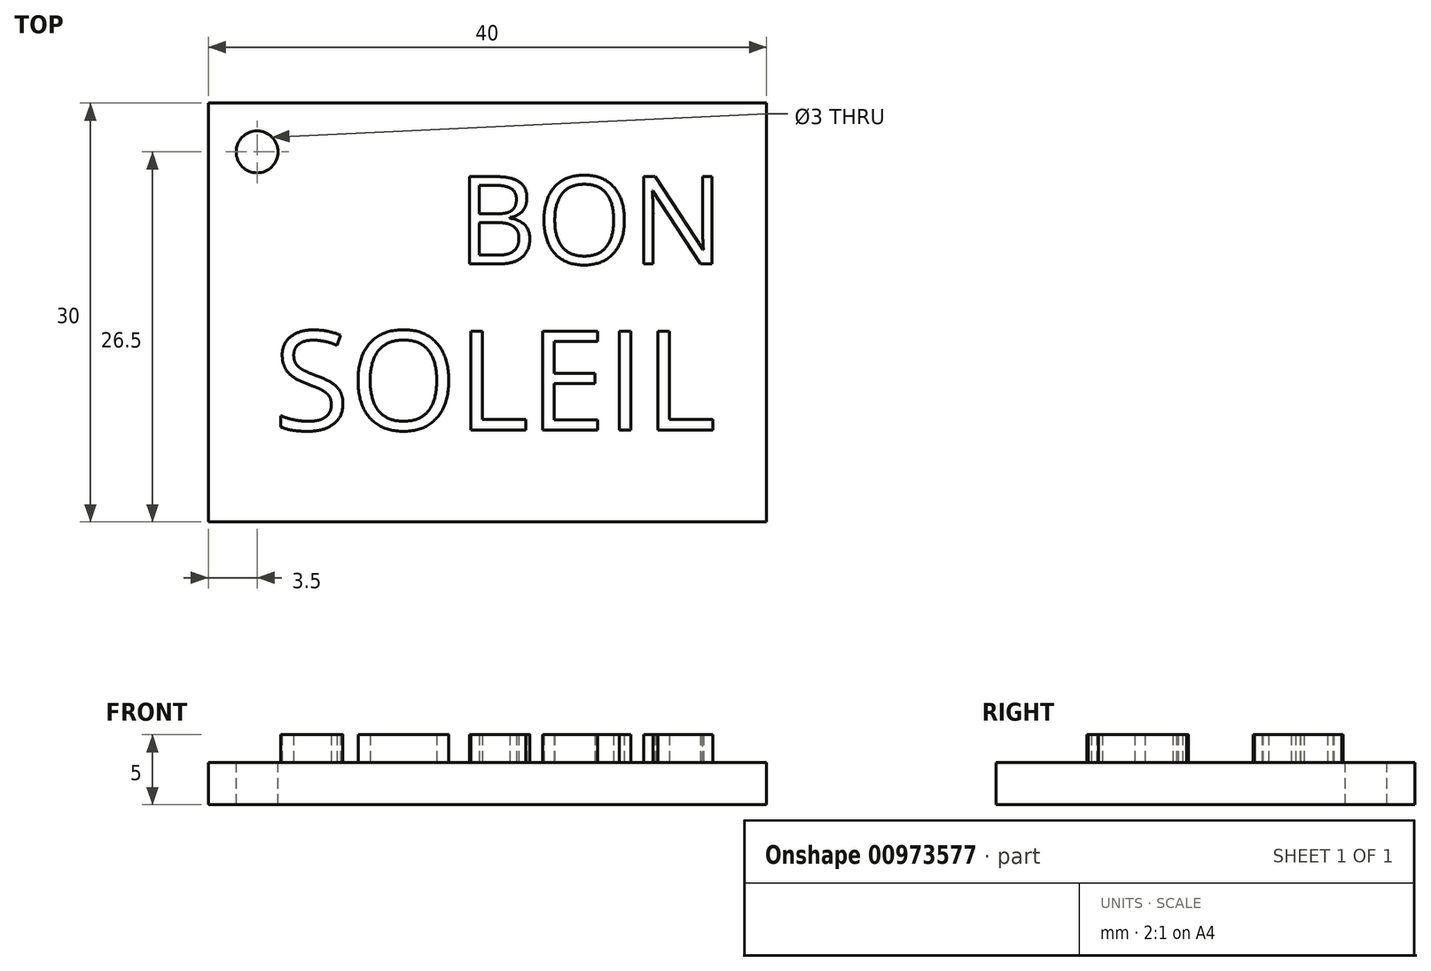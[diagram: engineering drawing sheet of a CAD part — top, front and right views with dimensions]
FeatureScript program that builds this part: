
annotation { "Feature Type Name" : "Feature", "Feature Type Description" : "" }
export const myFeature = defineFeature(function(context is Context, id is Id, definition is map)
    precondition{}
    {
        {
            var Q0;
            Q0=qCreatedBy(makeId("Top.planeOp"),FACE);
            var sketch = newSketch(context, id + "F0", { "sketchPlane" : qUnion([Q0])});
            skLineSegment(sketch, "E0.bottom", {"start": v(0, 0) * mm, "end": v(40, 0) * mm});
            skLineSegment(sketch, "E0.top", {"start": v(0, 30) * mm, "end": v(40, 30) * mm});
            skLineSegment(sketch, "E0.left", {"start": v(0, 0) * mm, "end": v(0, 30) * mm});
            skLineSegment(sketch, "E0.right", {"start": v(40, 0) * mm, "end": v(40, 30) * mm});
            skSolve(sketch);
        }
        {
            var Q0;
            Q0=qSketchRegion(id+"F0",true);
            extrude(context, id + "F1", {"entities" : qUnion([Q0]), "oppositeDirection" : true, "depth" : 3 * mm, "offsetDistance" : 25 * mm});
        }
        {
            var Q0;
            Q0=makeQuery(id+"F1.opExtrude","CAP_FACE",FACE,{"disambiguationData":[OSD([sQuery(id+"F0.wireOp",EDGE,"E0.bottom"),sQuery(id+"F0.wireOp",EDGE,"E0.top"),sQuery(id+"F0.wireOp",EDGE,"E0.left"),sQuery(id+"F0.wireOp",EDGE,"E0.right")])],"isStart":true});
            var sketch = newSketch(context, id + "F2", { "sketchPlane" : qUnion([Q0])});
            skText(sketch, "E1", { "text": "BON", "fontName": "OpenSans-Regular.ttf"});
            skText(sketch, "E2", { "text": "SOLEIL", "fontName": "OpenSans-Regular.ttf"});
            const initialGuessF2  = {"E1": [0.01784, 0.01848, 1, 0, 0.00631], "E2": [0.00469, 0.00658, 1, 0, 0.00713]};
            skSetInitialGuess(sketch, initialGuessF2);
            skSolve(sketch);
        }
        {
            var Q0;
            Q0=qSketchRegion(id+"F2",true);
            extrude(context, id + "F3", {"entities" : qUnion([Q0]), "operationType" : NewBodyOperationType.ADD, "depth" : 2 * mm, "offsetDistance" : 25 * mm});
        }
        {
            var Q0;
            {var subQ0=sQuery(id+"F0.wireOp",EDGE,"E0.top");var subQ1=sQuery(id+"F0.wireOp",EDGE,"E0.right");var subQ2=sQuery(id+"F0.wireOp",EDGE,"E0.bottom");var subQ3=sQuery(id+"F0.wireOp",EDGE,"E0.left");Q0=makeQuery(id+"F3.boolean.opBoolean","SPLIT",FACE,{"disambiguationData":[TD([makeQuery(id+"F1.opExtrude","SWEPT_FACE",FACE,{"disambiguationData":[OSD([subQ2])]})])],"derivedFrom":makeQuery(id+"F1.opExtrude","CAP_FACE",FACE,{"disambiguationData":[OSD([subQ2,subQ0,subQ3,subQ1])],"isStart":true})});}
            var sketch = newSketch(context, id + "F4", { "sketchPlane" : qUnion([Q0])});
            skCircle(sketch, "E3", {"center": v(3.5, 26.5) * mm, "radius": 1.5 * mm});
            skSolve(sketch);
        }
        {
            var Q0;
            Q0=qSketchRegion(id+"F4",true);
            extrude(context, id + "F5", {"entities" : qUnion([Q0]), "operationType" : NewBodyOperationType.REMOVE, "oppositeDirection" : true, "depth" : 4 * mm, "offsetDistance" : 25 * mm});
        }
    });
